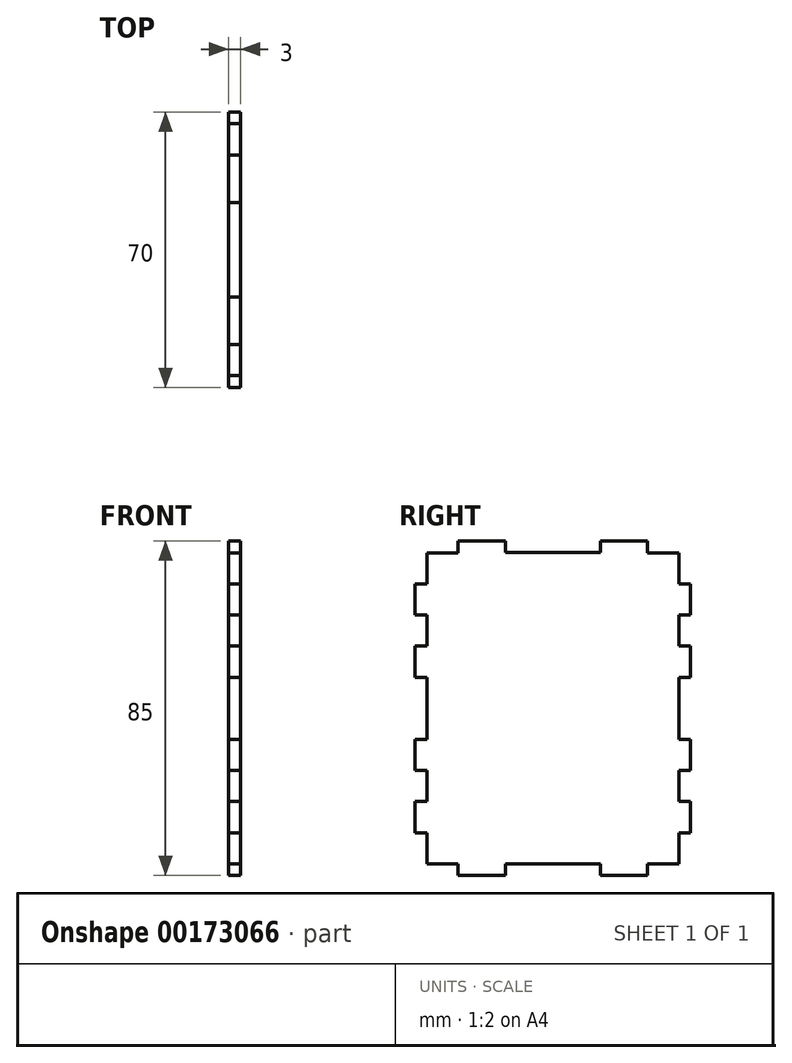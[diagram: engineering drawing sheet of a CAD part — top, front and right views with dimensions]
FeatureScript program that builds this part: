
annotation { "Feature Type Name" : "Feature", "Feature Type Description" : "" }
export const myFeature = defineFeature(function(context is Context, id is Id, definition is map)
    precondition{}
    {
        {
            var Q0;
            Q0=qCreatedBy(makeId("Right.planeOp"),FACE);
            var sketch = newSketch(context, id + "F0", { "sketchPlane" : qUnion([Q0])});
            skLineSegment(sketch, "E0.bottom", {"start": v(-24.1, 42.5) * mm, "end": v(-12.05, 42.5) * mm});
            skLineSegment(sketch, "E0.left", {"start": v(-35, 31.6) * mm, "end": v(-35, 23.7) * mm});
            skLineSegment(sketch, "E1.bottom", {"start": v(-32, 39.5) * mm, "end": v(-24.1, 39.5) * mm});
            skLineSegment(sketch, "E1.left", {"start": v(-32, 39.5) * mm, "end": v(-32, 31.6) * mm});
            skLineSegment(sketch, "E2", {"start": v(-35, 31.6) * mm, "end": v(-32, 31.6) * mm});
            skLineSegment(sketch, "E3", {"start": v(-35, 23.7) * mm, "end": v(-32, 23.7) * mm});
            skLineSegment(sketch, "E4", {"start": v(-35, 15.8) * mm, "end": v(-32, 15.8) * mm});
            skLineSegment(sketch, "E5", {"start": v(-35, 7.9) * mm, "end": v(-32, 7.9) * mm});
            skLineSegment(sketch, "E6", {"start": v(-24.1, 42.5) * mm, "end": v(-24.1, 39.5) * mm});
            skPoint(sketch, "E7.orphan", {"position": v(-35, 42.5) * mm});
            skLineSegment(sketch, "E8.trimOffspring", {"start": v(-35, 15.8) * mm, "end": v(-35, 7.9) * mm});
            skLineSegment(sketch, "E9", {"start": v(0, 39.5) * mm, "end": v(0, 0) * mm});
            skPoint(sketch, "E9.startSnap0", {"position": v(0, 39.5) * mm});
            skPoint(sketch, "E1.right.start.orphan", {"position": v(32, 39.5) * mm});
            skPoint(sketch, "E10.orphan", {"position": v(-32, -39.5) * mm});
            skPoint(sketch, "E11.start.orphan", {"position": v(-35, -31.6) * mm});
            skPoint(sketch, "E12.end.orphan", {"position": v(-32, -23.7) * mm});
            skPoint(sketch, "E13.orphan", {"position": v(-32, -15.8) * mm});
            skPoint(sketch, "E14.start.orphan", {"position": v(-35, -7.9) * mm});
            skPoint(sketch, "E15.orphan", {"position": v(-32, -7.9) * mm});
            skLineSegment(sketch, "E16.trimOffspring", {"start": v(-32, 23.7) * mm, "end": v(-32, 15.8) * mm});
            skLineSegment(sketch, "E17.trimOffspring", {"start": v(-32, 7.9) * mm, "end": v(-32, 0) * mm});
            skLineSegment(sketch, "E18.MirrorCS", {"start": v(24.1, 42.5) * mm, "end": v(24.1, 39.5) * mm});
            skLineSegment(sketch, "E19.MirrorCS", {"start": v(35, 15.8) * mm, "end": v(32, 15.8) * mm});
            skLineSegment(sketch, "E20.MirrorCS", {"start": v(35, 23.7) * mm, "end": v(32, 23.7) * mm});
            skLineSegment(sketch, "E21.MirrorCS", {"start": v(35, 7.9) * mm, "end": v(32, 7.9) * mm});
            skLineSegment(sketch, "E22.MirrorCS", {"start": v(35, 31.6) * mm, "end": v(32, 31.6) * mm});
            skLineSegment(sketch, "E23.MirrorCS", {"start": v(35, 15.8) * mm, "end": v(35, 7.9) * mm});
            skLineSegment(sketch, "E24.MirrorCS", {"start": v(32, 23.7) * mm, "end": v(32, 15.8) * mm});
            skLineSegment(sketch, "E25.MirrorCS", {"start": v(32, 7.9) * mm, "end": v(32, 0) * mm});
            skLineSegment(sketch, "E26.MirrorCS", {"start": v(32, 39.5) * mm, "end": v(32, 31.6) * mm});
            skPoint(sketch, "E27.MirrorP", {"position": v(35, 42.5) * mm});
            skLineSegment(sketch, "E28.MirrorCS", {"start": v(35, 31.6) * mm, "end": v(35, 23.7) * mm});
            skLineSegment(sketch, "E29.MirrorCS", {"start": v(32, 39.5) * mm, "end": v(24.1, 39.5) * mm});
            skLineSegment(sketch, "E30.MirrorCS", {"start": v(24.1, 42.5) * mm, "end": v(12.05, 42.5) * mm});
            skLineSegment(sketch, "E31", {"start": v(-12.05, 42.5) * mm, "end": v(-12.05, 39.57) * mm});
            skLineSegment(sketch, "E32", {"start": v(12.05, 42.5) * mm, "end": v(12.05, 39.57) * mm});
            skPoint(sketch, "E33.orphan", {"position": v(0, 42.5) * mm});
            skLineSegment(sketch, "E34.MirrorCS", {"start": v(35, -23.7) * mm, "end": v(32, -23.7) * mm});
            skLineSegment(sketch, "E35.MirrorCS", {"start": v(-35, -7.9) * mm, "end": v(-32, -7.9) * mm});
            skLineSegment(sketch, "E36.MirrorCS", {"start": v(-35, -23.7) * mm, "end": v(-32, -23.7) * mm});
            skLineSegment(sketch, "E37.MirrorCS", {"start": v(35, -15.8) * mm, "end": v(32, -15.8) * mm});
            skLineSegment(sketch, "E38.MirrorCS", {"start": v(-24.1, -42.5) * mm, "end": v(-24.1, -39.5) * mm});
            skLineSegment(sketch, "E39.MirrorCS", {"start": v(-35, -15.8) * mm, "end": v(-32, -15.8) * mm});
            skLineSegment(sketch, "E40.MirrorCS", {"start": v(35, -7.9) * mm, "end": v(32, -7.9) * mm});
            skLineSegment(sketch, "E41.MirrorCS", {"start": v(24.1, -42.5) * mm, "end": v(24.1, -39.5) * mm});
            skLineSegment(sketch, "E42.MirrorCS", {"start": v(35, -31.6) * mm, "end": v(32, -31.6) * mm});
            skLineSegment(sketch, "E43.MirrorCS", {"start": v(-12.05, -42.5) * mm, "end": v(-12.05, -39.57) * mm});
            skLineSegment(sketch, "E44.MirrorCS", {"start": v(-35, -31.6) * mm, "end": v(-32, -31.6) * mm});
            skPoint(sketch, "E45.MirrorP", {"position": v(0, -39.5) * mm});
            skLineSegment(sketch, "E46.MirrorCS", {"start": v(-32, -39.5) * mm, "end": v(-24.1, -39.5) * mm});
            skPoint(sketch, "E47.MirrorP", {"position": v(0, -42.5) * mm});
            skLineSegment(sketch, "E48.MirrorCS", {"start": v(32, -39.5) * mm, "end": v(32, -31.6) * mm});
            skLineSegment(sketch, "E49.MirrorCS", {"start": v(12.05, -42.5) * mm, "end": v(12.05, -39.57) * mm});
            skLineSegment(sketch, "E50.MirrorCS", {"start": v(32, -7.9) * mm, "end": v(32, 0) * mm});
            skLineSegment(sketch, "E51.MirrorCS", {"start": v(-32, -23.7) * mm, "end": v(-32, -15.8) * mm});
            skLineSegment(sketch, "E52.MirrorCS", {"start": v(-32, -39.5) * mm, "end": v(-32, -31.6) * mm});
            skLineSegment(sketch, "E53.MirrorCS", {"start": v(-35, -31.6) * mm, "end": v(-35, -23.7) * mm});
            skPoint(sketch, "E54.MirrorP", {"position": v(35, -42.5) * mm});
            skLineSegment(sketch, "E55.MirrorCS", {"start": v(-35, -15.8) * mm, "end": v(-35, -7.9) * mm});
            skPoint(sketch, "E56.MirrorP", {"position": v(32, -39.5) * mm});
            skPoint(sketch, "E57.MirrorP", {"position": v(-35, 7.9) * mm});
            skPoint(sketch, "E58.MirrorP", {"position": v(-35, -42.5) * mm});
            skLineSegment(sketch, "E59.MirrorCS", {"start": v(0, -39.5) * mm, "end": v(0, 0) * mm});
            skPoint(sketch, "E60.MirrorP", {"position": v(-32, 7.9) * mm});
            skLineSegment(sketch, "E61.MirrorCS", {"start": v(-32, -7.9) * mm, "end": v(-32, 0) * mm});
            skLineSegment(sketch, "E62.MirrorCS", {"start": v(32, -23.7) * mm, "end": v(32, -15.8) * mm});
            skLineSegment(sketch, "E63.MirrorCS", {"start": v(35, -31.6) * mm, "end": v(35, -23.7) * mm});
            skLineSegment(sketch, "E64.MirrorCS", {"start": v(32, -39.5) * mm, "end": v(24.1, -39.5) * mm});
            skLineSegment(sketch, "E65.MirrorCS", {"start": v(24.1, -42.5) * mm, "end": v(12.05, -42.5) * mm});
            skLineSegment(sketch, "E66.MirrorCS", {"start": v(35, -15.8) * mm, "end": v(35, -7.9) * mm});
            skLineSegment(sketch, "E67.MirrorCS", {"start": v(-24.1, -42.5) * mm, "end": v(-12.05, -42.5) * mm});
            skLineSegment(sketch, "E68", {"start": v(-12.05, 39.57) * mm, "end": v(12.05, 39.57) * mm});
            skPoint(sketch, "E69.orphan", {"position": v(12.05, 39.05) * mm});
            skLineSegment(sketch, "E70", {"start": v(-12.05, -39.57) * mm, "end": v(12.05, -39.57) * mm});
            skPoint(sketch, "E71.orphan", {"position": v(12.05, -39.05) * mm});
            skSolve(sketch);
        }
        {
            var Q0;
            Q0=qSketchRegion(id+"F0",true);
            extrude(context, id + "F1", {"entities" : qUnion([Q0]), "depth" : 3 * mm});
        }
    });
